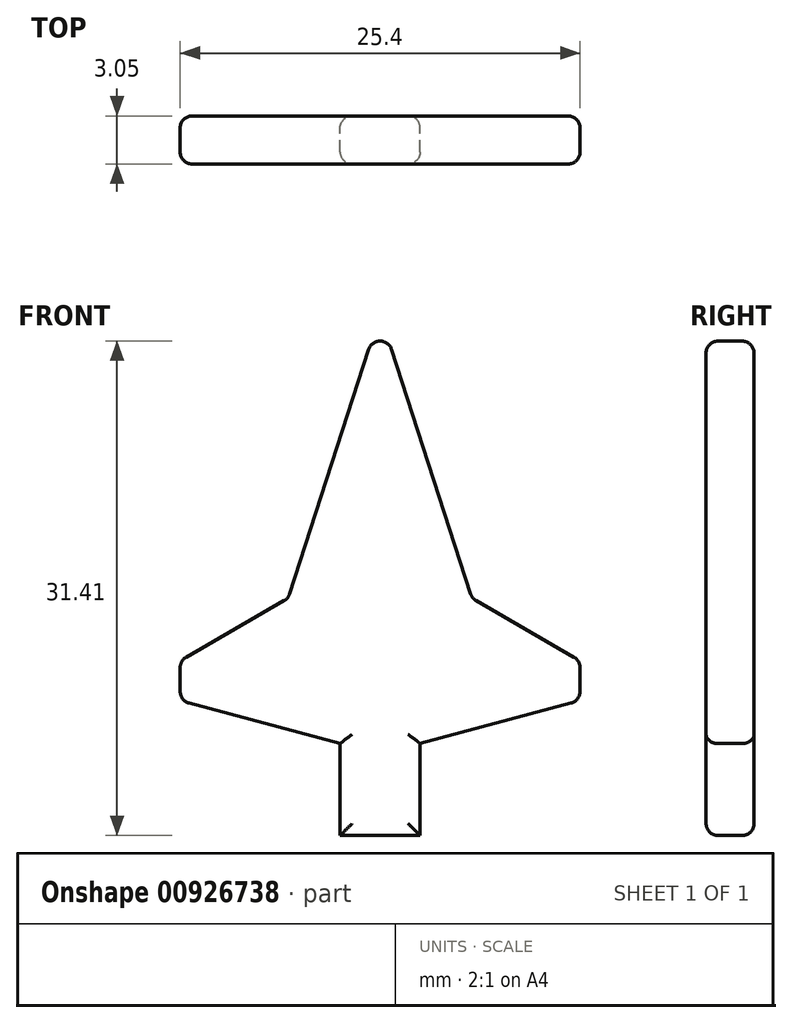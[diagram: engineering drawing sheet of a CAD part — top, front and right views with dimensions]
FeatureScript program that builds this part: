
annotation { "Feature Type Name" : "Feature", "Feature Type Description" : "" }
export const myFeature = defineFeature(function(context is Context, id is Id, definition is map)
    precondition{}
    {
        {
            var Q0;
            Q0=qCreatedBy(makeId("Front.planeOp"),FACE);
            var sketch = newSketch(context, id + "F0", { "sketchPlane" : qUnion([Q0])});
            skLineSegment(sketch, "E0", {"start": v(-5.84, 13.19) * mm, "end": v(0, 31.24) * mm});
            skLineSegment(sketch, "E1", {"start": v(0, 31.24) * mm, "end": v(5.84, 13.19) * mm});
            skLineSegment(sketch, "E2", {"start": v(-2.54, 3.97) * mm, "end": v(-2.54, -1.88) * mm});
            skLineSegment(sketch, "E3", {"start": v(-2.54, -1.88) * mm, "end": v(2.54, -1.88) * mm});
            skLineSegment(sketch, "E4", {"start": v(2.54, -1.88) * mm, "end": v(2.54, 3.97) * mm});
            skLineSegment(sketch, "E5", {"start": v(2.54, 3.97) * mm, "end": v(12.7, 6.69) * mm});
            skLineSegment(sketch, "E6", {"start": v(-2.54, 3.97) * mm, "end": v(-12.7, 6.69) * mm});
            skLineSegment(sketch, "E7", {"start": v(-12.7, 6.69) * mm, "end": v(-12.7, 9.23) * mm});
            skLineSegment(sketch, "E8", {"start": v(-12.7, 9.23) * mm, "end": v(-5.84, 13.19) * mm});
            skLineSegment(sketch, "E9", {"start": v(12.7, 6.69) * mm, "end": v(12.7, 9.23) * mm});
            skLineSegment(sketch, "E10", {"start": v(12.7, 9.23) * mm, "end": v(5.84, 13.19) * mm});
            skSolve(sketch);
        }
        {
            var Q0;
            Q0 = qSketchRegion(id + "F0", true);
            extrude(context, id + "F1", {"entities" : qUnion([Q0]), "depth" : 3.05 * mm, "offsetDistance" : 25.4 * mm});
        }
        {
            var Q0;
            Q0=makeQuery(id+"F1.opExtrude","SWEPT_EDGE",EDGE,{"disambiguationData":[OSD([sQuery(id+"F0.wireOp",EDGE,"E0"),sQuery(id+"F0.wireOp",EDGE,"E1")])]});
            var Q1;
            Q1=makeQuery(id+"F1.opExtrude","SWEPT_EDGE",EDGE,{"disambiguationData":[OSD([sQuery(id+"F0.wireOp",EDGE,"E1"),sQuery(id+"F0.wireOp",EDGE,"E10")])]});
            var Q2;
            Q2=makeQuery(id+"F1.opExtrude","SWEPT_EDGE",EDGE,{"disambiguationData":[OSD([sQuery(id+"F0.wireOp",EDGE,"E9"),sQuery(id+"F0.wireOp",EDGE,"E10")])]});
            var Q3;
            Q3=makeQuery(id+"F1.opExtrude","SWEPT_EDGE",EDGE,{"disambiguationData":[OSD([sQuery(id+"F0.wireOp",EDGE,"E5"),sQuery(id+"F0.wireOp",EDGE,"E9")])]});
            var Q4;
            Q4=makeQuery(id+"F1.opExtrude","SWEPT_EDGE",EDGE,{"disambiguationData":[OSD([sQuery(id+"F0.wireOp",EDGE,"E0"),sQuery(id+"F0.wireOp",EDGE,"E8")])]});
            var Q5;
            Q5=makeQuery(id+"F1.opExtrude","SWEPT_EDGE",EDGE,{"disambiguationData":[OSD([sQuery(id+"F0.wireOp",EDGE,"E7"),sQuery(id+"F0.wireOp",EDGE,"E8")])]});
            var Q6;
            Q6=makeQuery(id+"F1.opExtrude","SWEPT_EDGE",EDGE,{"disambiguationData":[OSD([sQuery(id+"F0.wireOp",EDGE,"E6"),sQuery(id+"F0.wireOp",EDGE,"E7")])]});
            var Q7;
            Q7=makeQuery(id+"F1.opExtrude","CAP_EDGE",EDGE,{"disambiguationData":[OSD([sQuery(id+"F0.wireOp",EDGE,"E4")])],"isStart":true});
            var Q8;
            Q8=makeQuery(id+"F1.opExtrude","CAP_EDGE",EDGE,{"disambiguationData":[OSD([sQuery(id+"F0.wireOp",EDGE,"E4")])],"isStart":false});
            var Q9;
            Q9=makeQuery(id+"F1.opExtrude","CAP_EDGE",EDGE,{"disambiguationData":[OSD([sQuery(id+"F0.wireOp",EDGE,"E2")])],"isStart":false});
            var Q10;
            Q10=makeQuery(id+"F1.opExtrude","CAP_EDGE",EDGE,{"disambiguationData":[OSD([sQuery(id+"F0.wireOp",EDGE,"E2")])],"isStart":true});
            var Q11;
            Q11=makeQuery(id+"F1.opExtrude","CAP_FACE",FACE,{"disambiguationData":[OSD([sQuery(id+"F0.wireOp",EDGE,"E0"),sQuery(id+"F0.wireOp",EDGE,"E1"),sQuery(id+"F0.wireOp",EDGE,"E2"),sQuery(id+"F0.wireOp",EDGE,"E3"),sQuery(id+"F0.wireOp",EDGE,"E4"),sQuery(id+"F0.wireOp",EDGE,"E5"),sQuery(id+"F0.wireOp",EDGE,"E6"),sQuery(id+"F0.wireOp",EDGE,"E7"),sQuery(id+"F0.wireOp",EDGE,"E8"),sQuery(id+"F0.wireOp",EDGE,"E9"),sQuery(id+"F0.wireOp",EDGE,"E10")])],"isStart":false});
            var Q12;
            Q12=makeQuery(id+"F1.opExtrude","CAP_FACE",FACE,{"disambiguationData":[OSD([sQuery(id+"F0.wireOp",EDGE,"E0"),sQuery(id+"F0.wireOp",EDGE,"E1"),sQuery(id+"F0.wireOp",EDGE,"E2"),sQuery(id+"F0.wireOp",EDGE,"E3"),sQuery(id+"F0.wireOp",EDGE,"E4"),sQuery(id+"F0.wireOp",EDGE,"E5"),sQuery(id+"F0.wireOp",EDGE,"E6"),sQuery(id+"F0.wireOp",EDGE,"E7"),sQuery(id+"F0.wireOp",EDGE,"E8"),sQuery(id+"F0.wireOp",EDGE,"E9"),sQuery(id+"F0.wireOp",EDGE,"E10")])],"isStart":true});
            fillet(context, id + "F2", {"entities" : qUnion([Q0, Q1, Q2, Q3, Q4, Q5, Q6, Q7, Q8, Q9, Q10, Q11, Q12]), "radius" : 0.76 * mm, "tangentPropagation" : true, "allowEdgeOverflow" : false});
        }
    });
